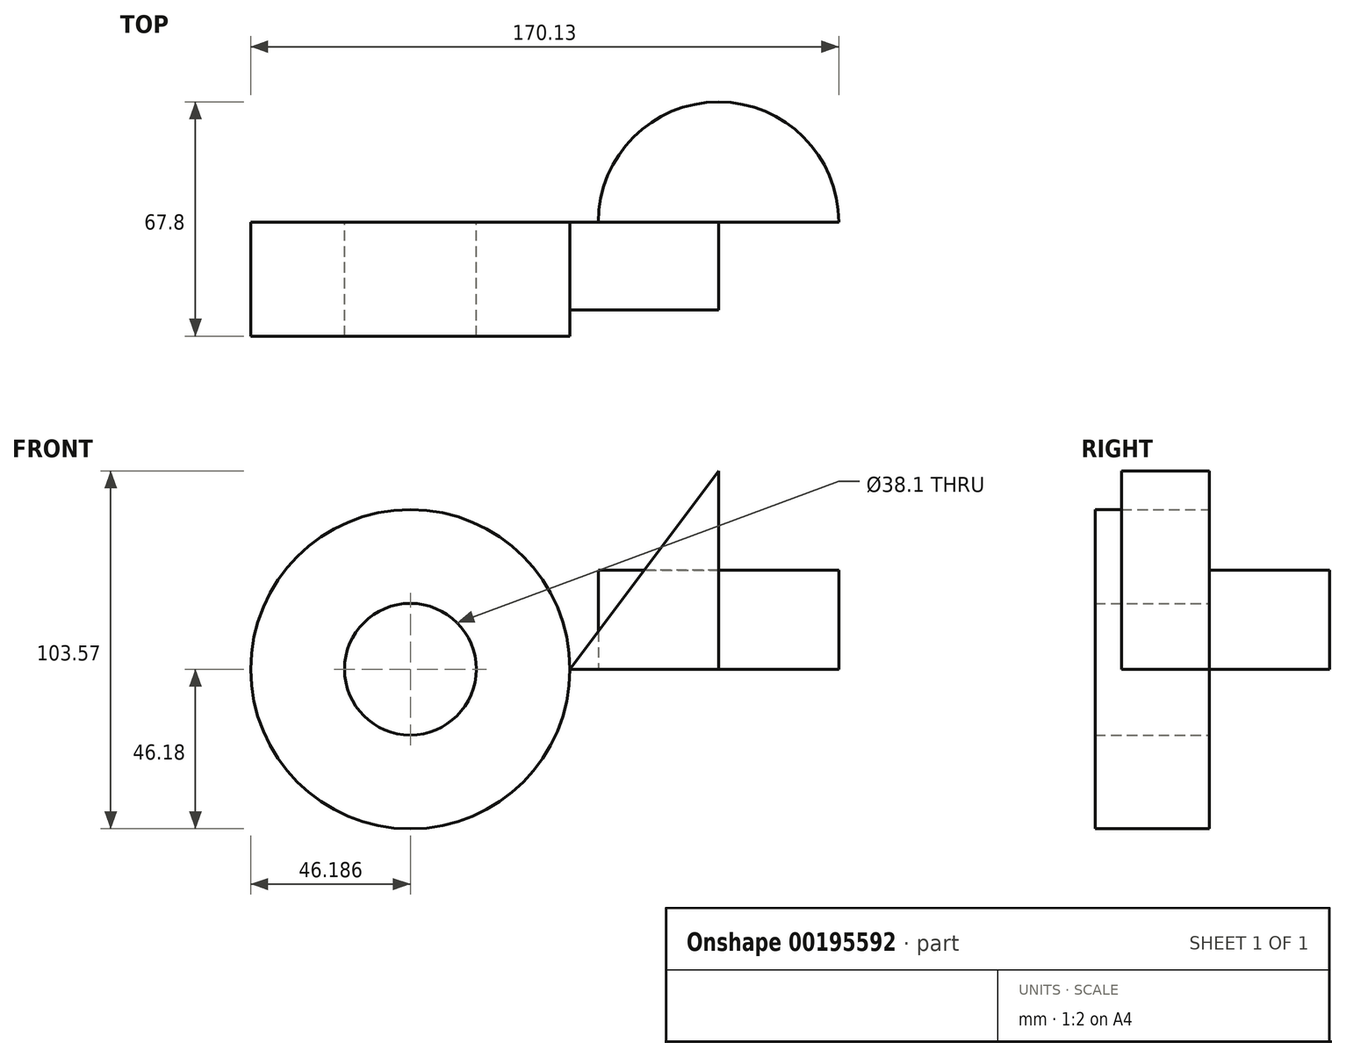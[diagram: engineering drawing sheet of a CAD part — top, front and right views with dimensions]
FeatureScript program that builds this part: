
annotation { "Feature Type Name" : "Feature", "Feature Type Description" : "" }
export const myFeature = defineFeature(function(context is Context, id is Id, definition is map)
    precondition{}
    {
        {
            var Q0;
            Q0=qCreatedBy(makeId("Front.planeOp"),FACE);
            var sketch = newSketch(context, id + "F6", { "sketchPlane" : qUnion([Q0])});
            skLineSegment(sketch, "E0", {"start": v(42.98, 57.4) * mm, "end": v(0, 0) * mm});
            skLineSegment(sketch, "E1", {"start": v(42.98, 57.4) * mm, "end": v(42.98, 0) * mm});
            skLineSegment(sketch, "E2", {"start": v(42.98, 0) * mm, "end": v(0, 0) * mm});
            skLineSegment(sketch, "E3.bottom", {"start": v(42.98, 28.7) * mm, "end": v(77.76, 28.7) * mm});
            skLineSegment(sketch, "E3.top", {"start": v(42.98, 0) * mm, "end": v(77.76, 0) * mm});
            skLineSegment(sketch, "E3.left", {"start": v(42.98, 28.7) * mm, "end": v(42.98, 0) * mm});
            skLineSegment(sketch, "E3.right", {"start": v(77.76, 28.7) * mm, "end": v(77.76, 0) * mm});
            skSolve(sketch);
        }
        {
            var Q0;
            Q0=qCreatedBy(makeId("Front.planeOp"),FACE);
            var sketch = newSketch(context, id + "F0", { "sketchPlane" : qUnion([Q0])});
            skCircle(sketch, "E4", {"center": v(-46.18, 0) * mm, "radius": 46.18 * mm});
            skSolve(sketch);
        }
        {
            var Q0;
            Q0=makeQuery(id+"F0.imprint","IMPRINT",FACE,{"disambiguationData":[TD([[makeQuery(id+"F0.imprint","IMPRINT",EDGE,{"derivedFrom":sQuery(id+"F0.wireOp",EDGE,"E4")}),1.0]])]});
            extrude(context, id + "F1", {"entities" : qUnion([Q0]), "depth" : 33.02 * mm});
        }
        {
            var Q0;
            Q0=makeQuery(id+"F6.imprint","IMPRINT",FACE,{"disambiguationData":[TD([[makeQuery(id+"F6.imprint","IMPRINT",EDGE,{"derivedFrom":sQuery(id+"F6.wireOp",EDGE,"E0")}),1.0]])]});
            extrude(context, id + "F2", {"entities" : qUnion([Q0]), "depth" : 25.4 * mm});
        }
        {
            var Q0;
            Q0=makeQuery(id+"F6.imprint","IMPRINT",FACE,{"disambiguationData":[TD([[makeQuery(id+"F6.imprint","IMPRINT",EDGE,{"derivedFrom":sQuery(id+"F6.wireOp",EDGE,"E3.bottom")}),-1.0]])]});
            var Q1;
            Q1=sQuery(id+"F6.wireOp",EDGE,"E1");
            revolve(context, id + "F3", {"operationType" : NewBodyOperationType.ADD, "entities" : qUnion([Q0]), "axis" : qUnion([Q1]), "revolveType" : RevolveType.ONE_DIRECTION, "oppositeDirection" : true, "angle" : 180 * degree});
        }
        {
            var Q0;
            Q0=makeQuery(id+"F0.imprint","IMPRINT",FACE,{"disambiguationData":[TD([[makeQuery(id+"F0.imprint","IMPRINT",EDGE,{"derivedFrom":sQuery(id+"F0.wireOp",EDGE,"E4")}),1.0]])]});
            var sketch = newSketch(context, id + "F4", { "sketchPlane" : qUnion([Q0])});
            skCircle(sketch, "E5", {"center": v(-46.18, 0) * mm, "radius": 19.05 * mm});
            skSolve(sketch);
        }
        {
            var Q0;
            Q0 = qSketchRegion(id + "F4", true);
            extrude(context, id + "F5", {"entities" : qUnion([Q0]), "operationType" : NewBodyOperationType.REMOVE, "endBound" : BoundingType.UP_TO_NEXT, "depth" : 25.4 * mm});
        }
    });
